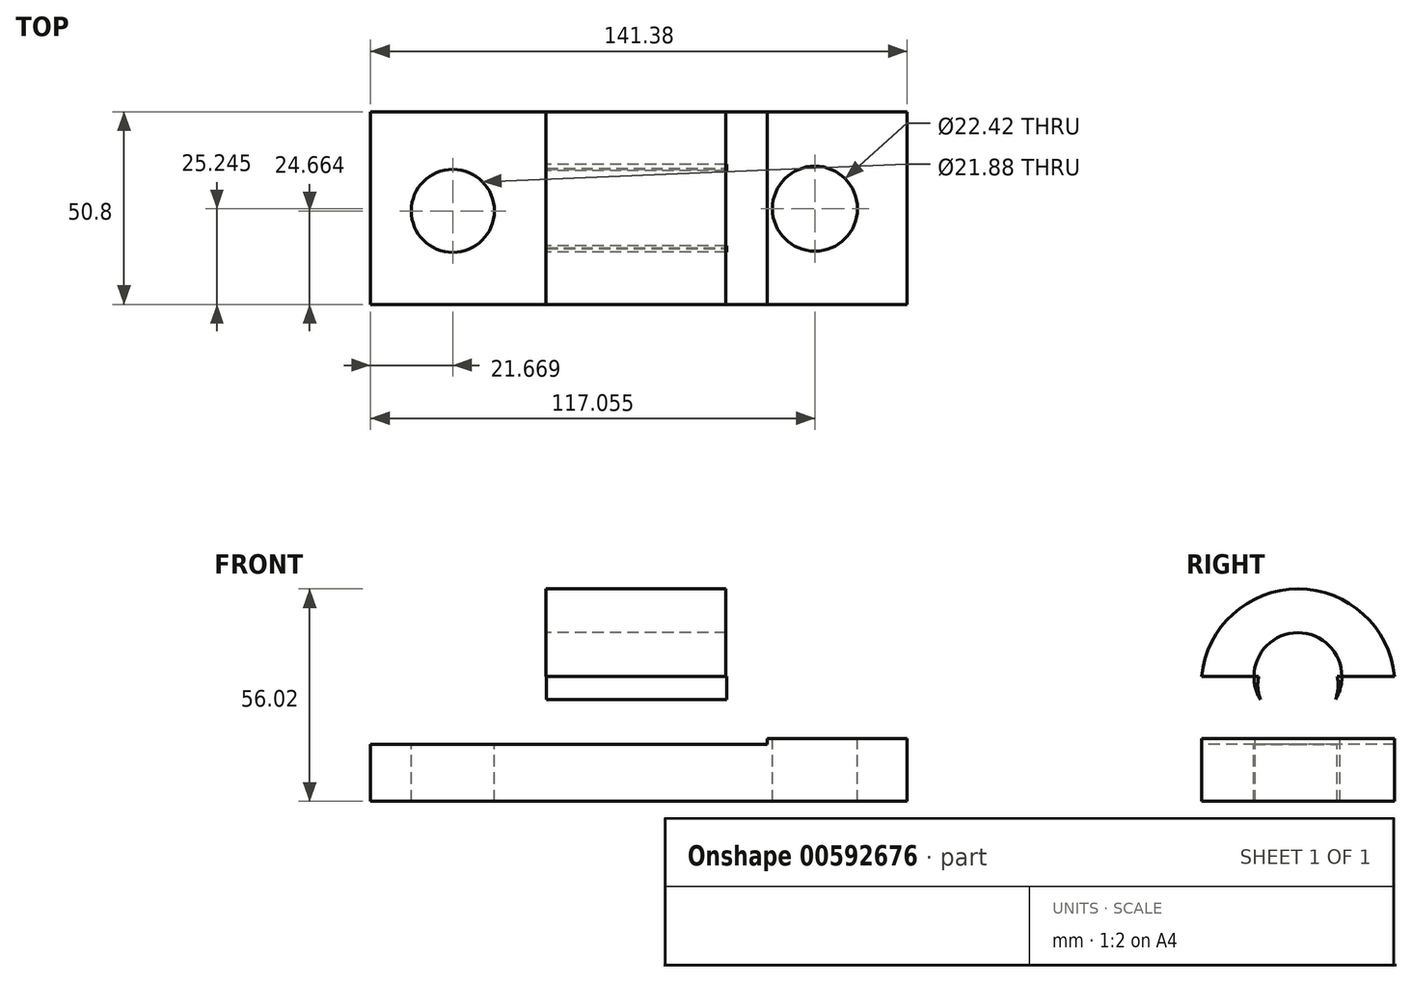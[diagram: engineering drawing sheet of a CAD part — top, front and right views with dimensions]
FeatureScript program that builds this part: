
annotation { "Feature Type Name" : "Feature", "Feature Type Description" : "" }
export const myFeature = defineFeature(function(context is Context, id is Id, definition is map)
    precondition{}
    {
        {
            var Q0;
            Q0=qCreatedBy(makeId("Front.planeOp"),FACE);
            var sketch = newSketch(context, id + "F0", { "sketchPlane" : qUnion([Q0])});
            skLineSegment(sketch, "E0", {"start": v(-74.58, 0) * mm, "end": v(-74.58, 30.86) * mm});
            skLineSegment(sketch, "E1", {"start": v(-74.58, 30.86) * mm, "end": v(0, 30.86) * mm});
            skLineSegment(sketch, "E2", {"start": v(0, 30.86) * mm, "end": v(0, 0) * mm});
            skLineSegment(sketch, "E3", {"start": v(0, 0) * mm, "end": v(-74.58, 0) * mm});
            skSolve(sketch);
        }
        {
            var Q0;
            Q0=makeQuery(id+"F0.imprint","IMPRINT",FACE,{"disambiguationData":[TD([[makeQuery(id+"F0.imprint","IMPRINT",EDGE,{"derivedFrom":sQuery(id+"F0.wireOp",EDGE,"E0")}),-1.0]])]});
            extrude(context, id + "F1", {"entities" : qUnion([Q0]), "depth" : 25.4 * mm, "offsetDistance" : 25.4 * mm});
        }
        {
            var Q0;
            Q0=makeQuery(id+"F1.opExtrude","SWEPT_FACE",FACE,{"disambiguationData":[OSD([sQuery(id+"F0.wireOp",EDGE,"E0")])]});
            extrude(context, id + "F2", {"entities" : qUnion([Q0]), "operationType" : NewBodyOperationType.ADD, "depth" : 25.4 * mm, "offsetDistance" : 25.4 * mm});
        }
        {
            var Q0;
            {var subQ0=sQuery(id+"F0.wireOp",EDGE,"E1");Q0=makeQuery(id+"F2.boolean.opBoolean","MERGE",FACE,{"derivedFrom":[makeQuery(id+"F1.opExtrude","SWEPT_FACE",FACE,{"disambiguationData":[OSD([subQ0])]}),makeQuery(id+"F2.opExtrude","SWEPT_FACE",FACE,{"disambiguationData":[OSD([sQuery(id+"F0.wireOp",EDGE,"E0"),subQ0])]})]});}
            extrude(context, id + "F3", {"entities" : qUnion([Q0]), "operationType" : NewBodyOperationType.ADD, "depth" : 25.4 * mm, "offsetDistance" : 25.4 * mm});
        }
        {
            var Q0;
            {var subQ0=sQuery(id+"F0.wireOp",EDGE,"E1");var subQ1=sQuery(id+"F0.wireOp",EDGE,"E0");Q0=makeQuery(id+"F3.boolean.opBoolean","MERGE",FACE,{"derivedFrom":[makeQuery(id+"F2.boolean.opBoolean","MERGE",FACE,{"derivedFrom":[makeQuery(id+"F1.opExtrude","CAP_FACE",FACE,{"disambiguationData":[OSD([subQ1,subQ0,sQuery(id+"F0.wireOp",EDGE,"E2"),sQuery(id+"F0.wireOp",EDGE,"E3")])],"isStart":false}),makeQuery(id+"F2.opExtrude","SWEPT_FACE",FACE,{"disambiguationData":[OSD([subQ1]),TDD([makeQuery(id+"F1.opExtrude","CAP_EDGE",EDGE,{"disambiguationData":[OSD([subQ1])],"isStart":false})])]})]}),makeQuery(id+"F3.opExtrude","SWEPT_FACE",FACE,{"disambiguationData":[OSD([subQ1,subQ0]),TDD([makeQuery(id+"F2.boolean.opBoolean","MERGE",EDGE,{"derivedFrom":[makeQuery(id+"F1.opExtrude","CAP_EDGE",EDGE,{"disambiguationData":[OSD([subQ0])],"isStart":false}),makeQuery(id+"F2.opExtrude","SWEPT_EDGE",EDGE,{"disambiguationData":[OSD([subQ1,subQ0]),TDD([makeQuery(id+"F1.opExtrude","CAP_VERTEX",VERTEX,{"disambiguationData":[OSD([subQ1,subQ0])],"isStart":false})])]})]})])]})]});}
            extrude(context, id + "F4", {"entities" : qUnion([Q0]), "operationType" : NewBodyOperationType.ADD, "depth" : 25.4 * mm, "offsetDistance" : 25.4 * mm});
        }
        {
            var Q0;
            {var subQ0=sQuery(id+"F0.wireOp",EDGE,"E1");var subQ1=sQuery(id+"F0.wireOp",EDGE,"E0");Q0=makeQuery(id+"F4.boolean.opBoolean","MERGE",FACE,{"derivedFrom":[makeQuery(id+"F3.boolean.opBoolean","MERGE",FACE,{"derivedFrom":[makeQuery(id+"F2.opExtrude","CAP_FACE",FACE,{"disambiguationData":[OSD([subQ1])],"isStart":false}),makeQuery(id+"F3.opExtrude","SWEPT_FACE",FACE,{"disambiguationData":[OSD([subQ1,subQ0]),TDD([makeQuery(id+"F2.opExtrude","CAP_EDGE",EDGE,{"disambiguationData":[OSD([subQ1,subQ0])],"isStart":false})])]})]}),makeQuery(id+"F4.opExtrude","SWEPT_FACE",FACE,{"disambiguationData":[OSD([subQ1,subQ0]),TDD([makeQuery(id+"F3.boolean.opBoolean","MERGE",EDGE,{"derivedFrom":[makeQuery(id+"F2.opExtrude","CAP_EDGE",EDGE,{"disambiguationData":[OSD([subQ1]),TDD([makeQuery(id+"F1.opExtrude","CAP_EDGE",EDGE,{"disambiguationData":[OSD([subQ1])],"isStart":false})])],"isStart":false}),makeQuery(id+"F3.opExtrude","SWEPT_EDGE",EDGE,{"disambiguationData":[OSD([subQ1,subQ0]),TDD([makeQuery(id+"F2.opExtrude","CAP_VERTEX",VERTEX,{"disambiguationData":[OSD([subQ1,subQ0]),TDD([makeQuery(id+"F1.opExtrude","CAP_VERTEX",VERTEX,{"disambiguationData":[OSD([subQ1,subQ0])],"isStart":false})])],"isStart":false})])]})]})])]})]});}
            var sketch = newSketch(context, id + "F5", { "sketchPlane" : qUnion([Q0])});
            skArc(sketch, "E4", {"start": v(50.8, 28.13) * mm, "mid": v(25.4, 56.02) * mm, "end": v(0, 28.13) * mm});
            skSolve(sketch);
        }
        {
            var Q0;
            {var subQ1=sQuery(id+"F0.wireOp",EDGE,"E1");var subQ2=sQuery(id+"F0.wireOp",EDGE,"E0");var subQ7=makeQuery(id+"F4.boolean.opBoolean","MERGE",EDGE,{"derivedFrom":[makeQuery(id+"F3.opExtrude","CAP_EDGE",EDGE,{"disambiguationData":[OSD([subQ2,subQ1]),TDD([makeQuery(id+"F2.opExtrude","CAP_EDGE",EDGE,{"disambiguationData":[OSD([subQ2,subQ1])],"isStart":false})])],"isStart":false}),makeQuery(id+"F4.opExtrude","SWEPT_EDGE",EDGE,{"disambiguationData":[OSD([subQ2,subQ1])]})]});Q0=makeQuery(id+"F5.imprint","IMPRINT",FACE,{"disambiguationData":[TD([[makeQuery(id+"F5.imprint","IMPRINT",EDGE,{"derivedFrom":subQ7}),1.0]])]});}
            extrude(context, id + "F6", {"entities" : qUnion([Q0]), "operationType" : NewBodyOperationType.REMOVE, "oppositeDirection" : true, "depth" : 25.4 * mm, "offsetDistance" : 25.4 * mm});
        }
        {
            var Q0;
            Q0=makeQuery(id+"F6.boolean.opBoolean","COPY",FACE,{"derivedFrom":makeQuery(id+"F6.opExtrude","CAP_FACE",FACE,{"disambiguationData":[OSD([sQuery(id+"F0.wireOp",EDGE,"E0"),sQuery(id+"F0.wireOp",EDGE,"E1"),sQuery(id+"F5.wireOp",EDGE,"E4")])],"isStart":false})});
            extrude(context, id + "F7", {"entities" : qUnion([Q0]), "operationType" : NewBodyOperationType.REMOVE, "oppositeDirection" : true, "depth" : 151.38 * mm, "offsetDistance" : 25.4 * mm});
        }
        {
            var Q0;
            {var subQ0=sQuery(id+"F0.wireOp",EDGE,"E2");var subQ1=sQuery(id+"F0.wireOp",EDGE,"E1");Q0=makeQuery(id+"F4.boolean.opBoolean","MERGE",FACE,{"derivedFrom":[makeQuery(id+"F3.boolean.opBoolean","MERGE",FACE,{"derivedFrom":[makeQuery(id+"F1.opExtrude","SWEPT_FACE",FACE,{"disambiguationData":[OSD([subQ0])]}),makeQuery(id+"F3.opExtrude","SWEPT_FACE",FACE,{"disambiguationData":[OSD([subQ1,subQ0])]})]}),makeQuery(id+"F4.opExtrude","SWEPT_FACE",FACE,{"disambiguationData":[OSD([subQ1,subQ0])]})]});}
            extrude(context, id + "F8", {"entities" : qUnion([Q0]), "operationType" : NewBodyOperationType.ADD, "depth" : 25.4 * mm, "offsetDistance" : 25.4 * mm});
        }
        {
            var Q0;
            {var subQ0=sQuery(id+"F0.wireOp",EDGE,"E2");var subQ1=sQuery(id+"F0.wireOp",EDGE,"E1");Q0=makeQuery(id+"F8.boolean.opBoolean","MERGE",FACE,{"derivedFrom":[makeQuery(id+"F4.opExtrude","CAP_FACE",FACE,{"disambiguationData":[OSD([sQuery(id+"F0.wireOp",EDGE,"E0"),subQ1,subQ0,sQuery(id+"F0.wireOp",EDGE,"E3")])],"isStart":false}),makeQuery(id+"F8.opExtrude","SWEPT_FACE",FACE,{"disambiguationData":[OSD([subQ1,subQ0]),TDD([makeQuery(id+"F4.opExtrude","CAP_EDGE",EDGE,{"disambiguationData":[OSD([subQ1,subQ0])],"isStart":false})])]})]});}
            var sketch = newSketch(context, id + "F9", { "sketchPlane" : qUnion([Q0])});
            skLineSegment(sketch, "E5", {"start": v(-60.73, 32.89) * mm, "end": v(-60.73, 15.04) * mm});
            skLineSegment(sketch, "E6", {"start": v(-60.73, 15.04) * mm, "end": v(-99.98, 15.04) * mm});
            skSolve(sketch);
        }
        {
            var Q0;
            {var subQ7=sQuery(id+"F9.wireOp",EDGE,"E5");Q0=makeQuery(id+"F9.imprint","IMPRINT",FACE,{"disambiguationData":[TD([[makeQuery(id+"F9.imprint","IMPRINT",EDGE,{"derivedFrom":subQ7}),1.0]])]});}
            var sketch = newSketch(context, id + "F10", { "sketchPlane" : qUnion([Q0])});
            skLineSegment(sketch, "E7", {"start": v(-13.29, 33.03) * mm, "end": v(-13.29, 16.6) * mm});
            skLineSegment(sketch, "E8", {"start": v(-13.29, 16.6) * mm, "end": v(25.79, 16.6) * mm});
            skSolve(sketch);
        }
        {
            var Q0;
            {var subQ7=sQuery(id+"F9.wireOp",EDGE,"E5");Q0=makeQuery(id+"F9.imprint","IMPRINT",FACE,{"disambiguationData":[TD([[makeQuery(id+"F9.imprint","IMPRINT",EDGE,{"derivedFrom":subQ7}),1.0]])]});}
            var sketch = newSketch(context, id + "F11", { "sketchPlane" : qUnion([Q0])});
            skLineSegment(sketch, "E9", {"start": v(-60.73, 32.4) * mm, "end": v(-60.73, 55.98) * mm});
            skLineSegment(sketch, "E10", {"start": v(-60.73, 55.98) * mm, "end": v(-13.6, 55.98) * mm});
            skLineSegment(sketch, "E11", {"start": v(-13.6, 55.98) * mm, "end": v(-13.6, 33.65) * mm});
            skLineSegment(sketch, "E12", {"start": v(-60.73, 32.4) * mm, "end": v(-13.6, 33.65) * mm});
            skSolve(sketch);
        }
        {
            var Q0;
            {var subQ0=sQuery(id+"F9.wireOp",EDGE,"E5");Q0=makeQuery(id+"F9.imprint","IMPRINT",FACE,{"disambiguationData":[TD([[makeQuery(id+"F9.imprint","IMPRINT",EDGE,{"derivedFrom":subQ0}),-1.0]])]});}
            extrude(context, id + "F12", {"entities" : qUnion([Q0]), "operationType" : NewBodyOperationType.REMOVE, "oppositeDirection" : true, "depth" : 60.2 * mm, "offsetDistance" : 25.4 * mm});
        }
        {
            var Q0;
            {var subQ0=sQuery(id+"F10.wireOp",EDGE,"E8");var subQ1=sQuery(id+"F10.wireOp",EDGE,"E7");var subQ2=makeQuery(id+"F10.imprint","INTERSECT",VERTEX,{"derivedFrom":[subQ1,subQ0]});Q0=makeQuery(id+"F10.imprint","IMPRINT",FACE,{"disambiguationData":[TD([[makeQuery(id+"F10.imprint","IMPRINT",EDGE,{"disambiguationData":[TD([[subQ2,-1.0]])],"derivedFrom":subQ0}),1.0]])]});}
            extrude(context, id + "F13", {"entities" : qUnion([Q0]), "operationType" : NewBodyOperationType.REMOVE, "oppositeDirection" : true, "depth" : 64.26 * mm, "offsetDistance" : 25.4 * mm});
        }
        {
            var Q0;
            {var subQ0=sQuery(id+"F5.wireOp",EDGE,"E4");var subQ2=sQuery(id+"F0.wireOp",EDGE,"E1");var subQ3=sQuery(id+"F0.wireOp",EDGE,"E0");Q0=makeQuery(id+"F12.boolean.opBoolean","SPLIT",FACE,{"disambiguationData":[TD([makeQuery(id+"F6.boolean.opBoolean","COPY",FACE,{"derivedFrom":makeQuery(id+"F6.opExtrude","SWEPT_FACE",FACE,{"disambiguationData":[OSD([subQ0])]})})])],"derivedFrom":makeQuery(id+"F4.boolean.opBoolean","MERGE",FACE,{"derivedFrom":[makeQuery(id+"F3.boolean.opBoolean","MERGE",FACE,{"derivedFrom":[makeQuery(id+"F2.opExtrude","CAP_FACE",FACE,{"disambiguationData":[OSD([subQ3])],"isStart":false}),makeQuery(id+"F3.opExtrude","SWEPT_FACE",FACE,{"disambiguationData":[OSD([subQ3,subQ2]),TDD([makeQuery(id+"F2.opExtrude","CAP_EDGE",EDGE,{"disambiguationData":[OSD([subQ3,subQ2])],"isStart":false})])]})]}),makeQuery(id+"F4.opExtrude","SWEPT_FACE",FACE,{"disambiguationData":[OSD([subQ3,subQ2]),TDD([makeQuery(id+"F3.boolean.opBoolean","MERGE",EDGE,{"derivedFrom":[makeQuery(id+"F2.opExtrude","CAP_EDGE",EDGE,{"disambiguationData":[OSD([subQ3]),TDD([makeQuery(id+"F1.opExtrude","CAP_EDGE",EDGE,{"disambiguationData":[OSD([subQ3])],"isStart":false})])],"isStart":false}),makeQuery(id+"F3.opExtrude","SWEPT_EDGE",EDGE,{"disambiguationData":[OSD([subQ3,subQ2]),TDD([makeQuery(id+"F2.opExtrude","CAP_VERTEX",VERTEX,{"disambiguationData":[OSD([subQ3,subQ2]),TDD([makeQuery(id+"F1.opExtrude","CAP_VERTEX",VERTEX,{"disambiguationData":[OSD([subQ3,subQ2])],"isStart":false})])],"isStart":false})])]})]})])]})]})});}
            extrude(context, id + "F14", {"entities" : qUnion([Q0]), "operationType" : NewBodyOperationType.REMOVE, "oppositeDirection" : true, "depth" : 39.12 * mm, "offsetDistance" : 25.4 * mm});
        }
        {
            var Q0;
            {var subQ0=sQuery(id+"F5.wireOp",EDGE,"E4");var subQ1=sQuery(id+"F0.wireOp",EDGE,"E2");var subQ2=sQuery(id+"F0.wireOp",EDGE,"E1");Q0=makeQuery(id+"F13.boolean.opBoolean","SPLIT",FACE,{"disambiguationData":[TD([makeQuery(id+"F6.boolean.opBoolean","COPY",FACE,{"derivedFrom":makeQuery(id+"F6.opExtrude","SWEPT_FACE",FACE,{"disambiguationData":[OSD([subQ0])]})})])],"derivedFrom":makeQuery(id+"F8.opExtrude","CAP_FACE",FACE,{"disambiguationData":[OSD([subQ2,subQ1])],"isStart":false})});}
            extrude(context, id + "F15", {"entities" : qUnion([Q0]), "operationType" : NewBodyOperationType.REMOVE, "oppositeDirection" : true, "depth" : 38.86 * mm, "offsetDistance" : 25.4 * mm});
        }
        {
            var Q0;
            {var subQ0=sQuery(id+"F0.wireOp",EDGE,"E3");var subQ1=sQuery(id+"F0.wireOp",EDGE,"E0");var subQ3=sQuery(id+"F0.wireOp",EDGE,"E1");Q0=makeQuery(id+"F12.boolean.opBoolean","SPLIT",FACE,{"disambiguationData":[TD([makeQuery(id+"F1.opExtrude","SWEPT_FACE",FACE,{"disambiguationData":[OSD([subQ0])]})])],"derivedFrom":makeQuery(id+"F4.boolean.opBoolean","MERGE",FACE,{"derivedFrom":[makeQuery(id+"F3.boolean.opBoolean","MERGE",FACE,{"derivedFrom":[makeQuery(id+"F2.opExtrude","CAP_FACE",FACE,{"disambiguationData":[OSD([subQ1])],"isStart":false}),makeQuery(id+"F3.opExtrude","SWEPT_FACE",FACE,{"disambiguationData":[OSD([subQ1,subQ3]),TDD([makeQuery(id+"F2.opExtrude","CAP_EDGE",EDGE,{"disambiguationData":[OSD([subQ1,subQ3])],"isStart":false})])]})]}),makeQuery(id+"F4.opExtrude","SWEPT_FACE",FACE,{"disambiguationData":[OSD([subQ1,subQ3]),TDD([makeQuery(id+"F3.boolean.opBoolean","MERGE",EDGE,{"derivedFrom":[makeQuery(id+"F2.opExtrude","CAP_EDGE",EDGE,{"disambiguationData":[OSD([subQ1]),TDD([makeQuery(id+"F1.opExtrude","CAP_EDGE",EDGE,{"disambiguationData":[OSD([subQ1])],"isStart":false})])],"isStart":false}),makeQuery(id+"F3.opExtrude","SWEPT_EDGE",EDGE,{"disambiguationData":[OSD([subQ1,subQ3]),TDD([makeQuery(id+"F2.opExtrude","CAP_VERTEX",VERTEX,{"disambiguationData":[OSD([subQ1,subQ3]),TDD([makeQuery(id+"F1.opExtrude","CAP_VERTEX",VERTEX,{"disambiguationData":[OSD([subQ1,subQ3])],"isStart":false})])],"isStart":false})])]})]})])]})]})});}
            extrude(context, id + "F16", {"entities" : qUnion([Q0]), "operationType" : NewBodyOperationType.ADD, "depth" : 25.4 * mm, "offsetDistance" : 25.4 * mm});
        }
        {
            var Q0;
            {var subQ0=sQuery(id+"F0.wireOp",EDGE,"E3");var subQ2=sQuery(id+"F0.wireOp",EDGE,"E2");var subQ3=sQuery(id+"F0.wireOp",EDGE,"E1");Q0=makeQuery(id+"F13.boolean.opBoolean","SPLIT",FACE,{"disambiguationData":[TD([makeQuery(id+"F1.opExtrude","SWEPT_FACE",FACE,{"disambiguationData":[OSD([subQ0])]})])],"derivedFrom":makeQuery(id+"F8.opExtrude","CAP_FACE",FACE,{"disambiguationData":[OSD([subQ3,subQ2])],"isStart":false})});}
            extrude(context, id + "F17", {"entities" : qUnion([Q0]), "operationType" : NewBodyOperationType.ADD, "depth" : 25.4 * mm, "offsetDistance" : 25.4 * mm});
        }
        {
            var Q0;
            Q0=makeQuery(id+"F13.boolean.opBoolean","COPY",FACE,{"derivedFrom":makeQuery(id+"F13.opExtrude","SWEPT_FACE",FACE,{"disambiguationData":[OSD([sQuery(id+"F10.wireOp",EDGE,"E7")])]})});
            var sketch = newSketch(context, id + "F18", { "sketchPlane" : qUnion([Q0])});
            skCircle(sketch, "E13", {"center": v(-25.46, 30.62) * mm, "radius": 10.58 * mm});
            skSolve(sketch);
        }
        {
            var Q0;
            {var subQ0=sQuery(id+"F18.wireOp",EDGE,"E13");var subQ1=makeQuery(id+"F13.boolean.opBoolean","COPY",EDGE,{"derivedFrom":makeQuery(id+"F13.opExtrude","SWEPT_EDGE",EDGE,{"disambiguationData":[OSD([sQuery(id+"F0.wireOp",EDGE,"E0"),sQuery(id+"F0.wireOp",EDGE,"E1"),sQuery(id+"F0.wireOp",EDGE,"E2"),sQuery(id+"F5.wireOp",EDGE,"E4"),sQuery(id+"F10.wireOp",EDGE,"E7")])]})});var subQ2=makeQuery(id+"F18.imprint","INTERSECT",VERTEX,{"disambiguationData":[OD(0.0)],"derivedFrom":[subQ1,subQ0]});Q0=makeQuery(id+"F18.imprint","IMPRINT",FACE,{"disambiguationData":[TD([[makeQuery(id+"F18.imprint","IMPRINT",EDGE,{"disambiguationData":[TD([[subQ2,1.0]])],"derivedFrom":subQ0}),1.0]])]});}
            extrude(context, id + "F19", {"entities" : qUnion([Q0]), "operationType" : NewBodyOperationType.REMOVE, "oppositeDirection" : true, "depth" : 107.44 * mm, "offsetDistance" : 25.4 * mm});
        }
        {
            var Q0;
            Q0=makeQuery(id+"F12.boolean.opBoolean","COPY",FACE,{"derivedFrom":makeQuery(id+"F12.opExtrude","SWEPT_FACE",FACE,{"disambiguationData":[OSD([sQuery(id+"F9.wireOp",EDGE,"E5")])]})});
            var sketch = newSketch(context, id + "F20", { "sketchPlane" : qUnion([Q0])});
            skCircle(sketch, "E14", {"center": v(25.46, 32.89) * mm, "radius": 11.58 * mm});
            skSolve(sketch);
        }
        {
            var Q0;
            {var subQ1=sQuery(id+"F5.wireOp",EDGE,"E4");var subQ2=sQuery(id+"F0.wireOp",EDGE,"E2");var subQ3=sQuery(id+"F0.wireOp",EDGE,"E1");var subQ4=sQuery(id+"F0.wireOp",EDGE,"E0");var subQ5=makeQuery(id+"F15.boolean.opBoolean","COPY",FACE,{"derivedFrom":makeQuery(id+"F15.opExtrude","SWEPT_FACE",FACE,{"disambiguationData":[OSD([subQ4,subQ3,subQ2,subQ1])]})});var subQ11=sQuery(id+"F9.wireOp",EDGE,"E5");var subQ12=makeQuery(id+"F12.boolean.opBoolean","COPY",FACE,{"derivedFrom":makeQuery(id+"F12.opExtrude","SWEPT_FACE",FACE,{"disambiguationData":[OSD([subQ11])]})});var subQ13=makeQuery(id+"F19.opExtrude","SWEPT_FACE",FACE,{"disambiguationData":[OSD([subQ4,subQ3,subQ2,subQ1,sQuery(id+"F10.wireOp",EDGE,"E7")])]});var subQ16=makeQuery(id+"F12.boolean.opBoolean","COPY",EDGE,{"derivedFrom":makeQuery(id+"F12.opExtrude","SWEPT_EDGE",EDGE,{"disambiguationData":[OSD([subQ4,subQ3,subQ2,subQ1,subQ11])]})});var subQ24=makeQuery(id+"F19.boolean.opBoolean","SPLIT",EDGE,{"disambiguationData":[topologyDisambiguationEdgeConnected([subQ12,subQ5,subQ13])],"derivedFrom":subQ16});Q0=makeQuery(id+"F20.imprint","IMPRINT",FACE,{"disambiguationData":[TD([[makeQuery(id+"F20.imprint","IMPRINT",EDGE,{"derivedFrom":subQ24}),1.0]])]});}
            var Q1;
            {var subQ1=sQuery(id+"F5.wireOp",EDGE,"E4");var subQ2=sQuery(id+"F0.wireOp",EDGE,"E2");var subQ3=sQuery(id+"F0.wireOp",EDGE,"E1");var subQ4=sQuery(id+"F0.wireOp",EDGE,"E0");var subQ5=makeQuery(id+"F15.boolean.opBoolean","COPY",FACE,{"derivedFrom":makeQuery(id+"F15.opExtrude","SWEPT_FACE",FACE,{"disambiguationData":[OSD([subQ4,subQ3,subQ2,subQ1])]})});var subQ11=sQuery(id+"F9.wireOp",EDGE,"E5");var subQ12=makeQuery(id+"F12.boolean.opBoolean","COPY",FACE,{"derivedFrom":makeQuery(id+"F12.opExtrude","SWEPT_FACE",FACE,{"disambiguationData":[OSD([subQ11])]})});var subQ13=makeQuery(id+"F19.opExtrude","SWEPT_FACE",FACE,{"disambiguationData":[OSD([subQ4,subQ3,subQ2,subQ1,sQuery(id+"F10.wireOp",EDGE,"E7")])]});var subQ16=makeQuery(id+"F12.boolean.opBoolean","COPY",EDGE,{"derivedFrom":makeQuery(id+"F12.opExtrude","SWEPT_EDGE",EDGE,{"disambiguationData":[OSD([subQ4,subQ3,subQ2,subQ1,subQ11])]})});var subQ24=makeQuery(id+"F19.boolean.opBoolean","SPLIT",EDGE,{"disambiguationData":[topologyDisambiguationEdgeConnected([subQ12,subQ5,subQ13])],"derivedFrom":subQ16});Q1=makeQuery(id+"F20.imprint","IMPRINT",FACE,{"disambiguationData":[TD([[makeQuery(id+"F20.imprint","IMPRINT",EDGE,{"derivedFrom":subQ24}),-1.0]])]});}
            extrude(context, id + "F21", {"entities" : qUnion([Q0, Q1]), "operationType" : NewBodyOperationType.REMOVE, "oppositeDirection" : true, "depth" : 58.17 * mm, "offsetDistance" : 25.4 * mm});
        }
        {
            var Q0;
            Q0=makeQuery(id+"F21.boolean.opBoolean","COPY",FACE,{"derivedFrom":makeQuery(id+"F21.opExtrude","CAP_FACE",FACE,{"disambiguationData":[OSD([sQuery(id+"F20.wireOp",EDGE,"E14")])],"isStart":true})});
            extrude(context, id + "F22", {"entities" : qUnion([Q0]), "operationType" : NewBodyOperationType.REMOVE, "depth" : 25.4 * mm, "offsetDistance" : 25.4 * mm});
        }
        {
            var Q0;
            Q0=makeQuery(id+"F21.boolean.opBoolean","COPY",FACE,{"derivedFrom":makeQuery(id+"F21.opExtrude","CAP_FACE",FACE,{"disambiguationData":[OSD([sQuery(id+"F20.wireOp",EDGE,"E14")])],"isStart":true})});
            extrude(context, id + "F23", {"entities" : qUnion([Q0]), "operationType" : NewBodyOperationType.REMOVE, "oppositeDirection" : true, "depth" : 25.4 * mm, "offsetDistance" : 25.4 * mm});
        }
        {
            var Q0;
            Q0=makeQuery(id+"F17.opExtrude","CAP_FACE",FACE,{"disambiguationData":[OSD([sQuery(id+"F0.wireOp",EDGE,"E1"),sQuery(id+"F0.wireOp",EDGE,"E2")])],"isStart":false});
            extrude(context, id + "F24", {"entities" : qUnion([Q0]), "operationType" : NewBodyOperationType.REMOVE, "oppositeDirection" : true, "depth" : 16.5 * mm, "offsetDistance" : 25.4 * mm});
        }
        {
            var Q0;
            Q0=makeQuery(id+"F16.opExtrude","CAP_FACE",FACE,{"disambiguationData":[OSD([sQuery(id+"F0.wireOp",EDGE,"E0"),sQuery(id+"F0.wireOp",EDGE,"E1")])],"isStart":false});
            extrude(context, id + "F25", {"entities" : qUnion([Q0]), "operationType" : NewBodyOperationType.REMOVE, "oppositeDirection" : true, "depth" : 18.29 * mm, "offsetDistance" : 25.4 * mm});
        }
        {
            var Q0;
            {var subQ0=sQuery(id+"F10.wireOp",EDGE,"E8");Q0=makeQuery(id+"F17.boolean.opBoolean","MERGE",FACE,{"derivedFrom":[makeQuery(id+"F13.boolean.opBoolean","COPY",FACE,{"derivedFrom":makeQuery(id+"F13.opExtrude","SWEPT_FACE",FACE,{"disambiguationData":[OSD([subQ0])]})}),makeQuery(id+"F17.opExtrude","SWEPT_FACE",FACE,{"disambiguationData":[OSD([sQuery(id+"F0.wireOp",EDGE,"E1"),sQuery(id+"F0.wireOp",EDGE,"E2"),subQ0])]})]});}
            var sketch = newSketch(context, id + "F26", { "sketchPlane" : qUnion([Q0])});
            skCircle(sketch, "E15", {"center": v(9.97, -25.55) * mm, "radius": 11.21 * mm});
            skCircle(sketch, "E16", {"center": v(-84.31, -26) * mm, "radius": 10.53 * mm});
            skSolve(sketch);
        }
        {
            var Q0;
            Q0=makeQuery(id+"F26.imprint","IMPRINT",FACE,{"disambiguationData":[TD([[makeQuery(id+"F26.imprint","IMPRINT",EDGE,{"derivedFrom":sQuery(id+"F26.wireOp",EDGE,"E15")}),1.0]])]});
            extrude(context, id + "F27", {"entities" : qUnion([Q0]), "operationType" : NewBodyOperationType.REMOVE, "oppositeDirection" : true, "depth" : 45.72 * mm, "offsetDistance" : 25.4 * mm});
        }
        {
            var Q0;
            {var subQ0=sQuery(id+"F9.wireOp",EDGE,"E6");Q0=makeQuery(id+"F16.boolean.opBoolean","MERGE",FACE,{"derivedFrom":[makeQuery(id+"F12.boolean.opBoolean","COPY",FACE,{"derivedFrom":makeQuery(id+"F12.opExtrude","SWEPT_FACE",FACE,{"disambiguationData":[OSD([subQ0])]})}),makeQuery(id+"F16.opExtrude","SWEPT_FACE",FACE,{"disambiguationData":[OSD([sQuery(id+"F0.wireOp",EDGE,"E0"),sQuery(id+"F0.wireOp",EDGE,"E1"),subQ0])]})]});}
            var sketch = newSketch(context, id + "F28", { "sketchPlane" : qUnion([Q0])});
            skCircle(sketch, "E17", {"center": v(-85.42, -26.14) * mm, "radius": 10.94 * mm});
            skSolve(sketch);
        }
        {
            var Q0;
            Q0=makeQuery(id+"F28.imprint","IMPRINT",FACE,{"disambiguationData":[TD([[makeQuery(id+"F28.imprint","IMPRINT",EDGE,{"derivedFrom":sQuery(id+"F28.wireOp",EDGE,"E17")}),1.0]])]});
            extrude(context, id + "F29", {"entities" : qUnion([Q0]), "operationType" : NewBodyOperationType.REMOVE, "oppositeDirection" : true, "depth" : 60.45 * mm, "offsetDistance" : 25.4 * mm});
        }
    });
